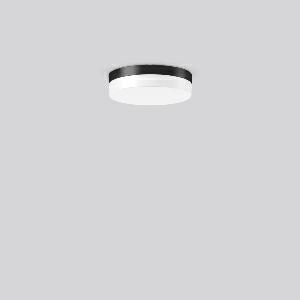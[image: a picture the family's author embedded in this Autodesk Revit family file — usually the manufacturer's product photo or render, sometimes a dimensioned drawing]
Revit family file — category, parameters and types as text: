
# Revit family: flat_slim_round_312132_0031_1_76_b503
name_source: partatom
category: Lighting Fixtures
units: mm (PartAtom-declared; Revit-internal decimal feet)

## family parameters
Cut with Voids When Loaded = No
Host = Face
Light Source = No
Part Type = Normal
Room Calculation Point = No
Round Connector Dimension = Use Diameter
Shared = No

## types (1)
- FLAT SLIM round (1 x LED Modul 840, 1000 lm, 4000)
    Apparent Load = 13 VA
    CIE Flux Codes = 42 72 92 89 100
    Color Rendering = 80
    Color Temperature = 4000
    Default Elevation = 1800 mm
    Height = 63 mm
    Lamp = 1 x LED Modul 840
    Lamp Light Flux = 1000 lm
    Lamp count = 1
    Length = 230 mm
    Lifetime = 50000 h
    Luminous efficacy = 77 lm/W
    Manufacturer = RZB
    ModVariant = No
    Model = 312132.0031.1.76
    Mounting Place = Ceiling, Wall
    Mounting Type = Surface mounted
    Number of Poles = 1
    OnlyDefault = Yes
    Power Factor = 1
    Product Name = FLAT SLIM round
    Product group = Surface mounted ceiling and wall luminaires
    ProductGroupID = 305
    Protection Class = Protection class I
    Protection Degree = IP 65
    RLX_Detail_Level = 1
    RLX_Emergency_Light_Flux = 0 lm
    RLX_Emergency_Type = 0
    RLX_Emergency_Type_DB = No
    RlxData = <blob elided: 17917 chars, md5=efd089bb>
    Socket = socket
    Standby Power = 0 W
    System Light Flux = 1000 lm
    System Power = 13 W
    Type Comments = Product without accessories
    Type Image = 312132.0031.jpg
    URL = http://relux.com
    VarID = ---
    Voltage = 230 V
    Voltage Range = 220-240 V
    Weight = 0.00 kg
    Width = 0 mm  [stored 0 ft]

note: [stored X ft] marks values corroborated as IEEE doubles in the binary element streams (Revit-internal decimal feet)

## geometry (parser evidence)
native form markers: Blend x4, Sweep x14
no freeform markers — native parametric forms only
